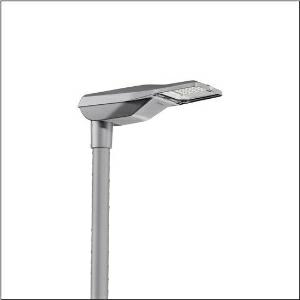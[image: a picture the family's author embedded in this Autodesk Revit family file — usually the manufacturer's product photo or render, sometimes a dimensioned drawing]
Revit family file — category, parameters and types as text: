
# Revit family: streetlight_sl_21_iq_micro___p0_8a_5xe1u31d08cb_216c
name_source: partatom
category: Lighting Fixtures
units: mm (PartAtom-declared; Revit-internal decimal feet)

## family parameters
Cut with Voids When Loaded = No
Host = Face
Light Source = No
Part Type = Normal
Room Calculation Point = No
Round Connector Dimension = Use Diameter
Shared = No

## types (1)
- --- (1 x LED, 2830 lm, 19.4 W, 3000K)
    Apparent Load = 19 VA
    CIE Flux Codes = 33 69 96 100 100
    Color Rendering = 70
    Color Temperature = 3000K
    Default Elevation = 1800 mm
    Description = Streetlight SL 21 iQ micro, mast luminaire, primary light control with lens, of PMMA, primary optical cover: cover, of toughened safety glass, transparent, light distribution: P0.8a, light emission: direct distribution, primary light characteristic: asymmetric, installation type: post-top, side-entry, LED, High Power LED, rated luminous flux: 2.830lm, luminous efficacy: 146lm/W, light colour: 730, colour temperature: 3000K, control gear: iQ-Comfort, control: pre-setting: linear dimming characteristic, Auto-Match, Temp-Guard, Lumen-Switch, Night-Set, Smart-Wire, Light-Fading, Desk-Remote (wireless, voltage-free reading and setting of iQ features in the workshop via application-optimized NFC function/RFID function), optimised constant luminous flux control (CLO 2.0), mains connection: 220..240V, AC, 50/60Hz, start of lifetime: 19W, end of service life: 20W, reduction: 10W, luminaire housing, of diecast aluminium, powder-coated, Siteco® metallic grey (DB 702S), corrosivity category C5 mid according to DIN EN ISO 12944, please order mast flange separately, inclination adjustable: 0°, 5°, 10°, 15°, sealing non-destructively replaceable, multi-level sealing system, length: 528mm, width: 235mm, height: 110mm, mast flange for spigot size: 42mm (side-entry): 5XC10008XM4, 60/48mm (side-entry/post-top): 5XC10108XM2, 76/60mm (side-entry/post-top): 5XC10108XM1, protection rating (complete): IP66, insulation class (complete): insulation class II (safety insulation), certification: CE, ENEC, ENEC+, VDE, impact resistance: IK09, permissible operating ambient temperature for outdoor applications: -40..+50°C, standard-compliant lighting for roads and squares, packaging unit: 1 piece

Light Distribution: P0.8a
    Height = 110 mm
    Lamp = 1 x LED
    Lamp Light Flux = 2830 lm
    Lamp Power = 19.4 W
    Lamp count = 1
    Length = 528 mm
    Luminous efficacy = 146 lm/W
    Manufacturer = Siteco
    ModVariant = No
    Model = 5XE1U31D08CB
    Number of Poles = 1
    OnlyDefault = Yes
    Power Factor = 1
    Product Name = Streetlight SL 21 iQ micro | P0.8a
    Product group = mast luminaire | pylon top
    ProductGroupID = 6100
    Protection Class = Protection class II
    Protection Degree = IP 66
    RLX_Detail_Level = 1
    RLX_Emergency_Light_Flux = 0 lm
    RLX_Emergency_Type = 0
    RLX_Emergency_Type_DB = No
    RlxData = <blob elided: 98709 chars, md5=25be0660>
    Socket = socket
    Standby Power = 0 W
    System Light Flux = 2830 lm
    System Power = 19 W
    Type Comments = factory setting: luminous flux: 100 % | dim-lin: 254 | 387 mA
    Type Image = l_1006881.jpg
    URL = http://relux.com
    VarID = @adj_070008
    Voltage = 0 V
    Weight = 0.00 kg
    Width = 235 mm

## geometry (parser evidence)
native form markers: Blend x4, Sweep x10
no freeform markers — native parametric forms only
